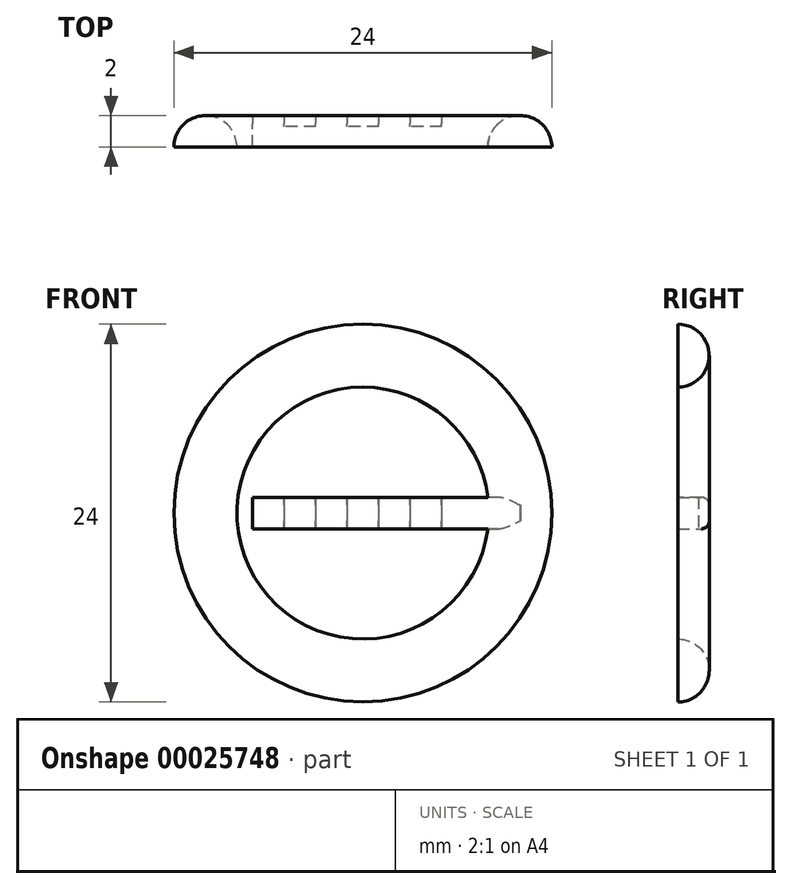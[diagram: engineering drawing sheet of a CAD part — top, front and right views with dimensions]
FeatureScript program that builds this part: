
annotation { "Feature Type Name" : "Feature", "Feature Type Description" : "" }
export const myFeature = defineFeature(function(context is Context, id is Id, definition is map)
    precondition{}
    {
        {
            var Q0;
            Q0=qCreatedBy(makeId("Top.planeOp"),FACE);
            var sketch = newSketch(context, id + "F0", { "sketchPlane" : qUnion([Q0])});
            skLineSegment(sketch, "E0", {"start": v(-2, 0) * mm, "end": v(2, 0) * mm});
            skArc(sketch, "E1", {"start": v(2, 0) * mm, "mid": v(0, 2) * mm, "end": v(-2, 0) * mm});
            skLineSegment(sketch, "E2", {"start": v(0, 0) * mm, "end": v(-17, 0) * mm});
            skSolve(sketch);
        }
        {
            var Q0;
            Q0=qCreatedBy(makeId("Front.planeOp"),FACE);
            var sketch = newSketch(context, id + "F1", { "sketchPlane" : qUnion([Q0])});
            skLineSegment(sketch, "E3", {"start": v(0, 0) * mm, "end": v(-20, 0) * mm, "construction": true});
            skCircle(sketch, "E4", {"center": v(-10, 0) * mm, "radius": 10 * mm, "construction": true});
            skSolve(sketch);
        }
        {
            var Q0;
            Q0=qCreatedBy(makeId("Right.planeOp"),FACE);
            var sketch = newSketch(context, id + "F2", { "sketchPlane" : qUnion([Q0])});
            skLineSegment(sketch, "E5.bottom", {"start": v(0, 1) * mm, "end": v(1.5, 1) * mm});
            skLineSegment(sketch, "E5.top", {"start": v(0, -1) * mm, "end": v(1.5, -1) * mm});
            skLineSegment(sketch, "E5.left", {"start": v(0, 1) * mm, "end": v(0, -1) * mm});
            skLineSegment(sketch, "E5.right", {"start": v(2, 0.5) * mm, "end": v(2, -0.5) * mm});
            skPoint(sketch, "E6.visualSharp", {"position": v(2, -1) * mm});
            skArc(sketch, "E6.filletArc", {"start": v(1.5, -1) * mm, "mid": v(1.85, -0.85) * mm, "end": v(2, -0.5) * mm});
            skPoint(sketch, "E7.visualSharp", {"position": v(2, 1) * mm});
            skArc(sketch, "E7.filletArc", {"start": v(2, 0.5) * mm, "mid": v(1.85, 0.85) * mm, "end": v(1.5, 1) * mm});
            skSolve(sketch);
        }
        {
            var Q0;
            {var subQ2=sQuery(id+"F0.wireOp",EDGE,"E0");Q0=makeQuery(id+"F0.imprint","IMPRINT",FACE,{"disambiguationData":[TD([[makeQuery(id+"F0.imprint","IMPRINT",EDGE,{"derivedFrom":subQ2}),1.0]])]});}
            var Q1;
            Q1=sQuery(id+"F0.wireOp",EDGE,"E1");
            var Q2;
            Q2=sQuery(id+"F0.wireOp",EDGE,"E0");
            var Q3;
            Q3=sQuery(id+"F1.wireOp",EDGE,"E4");
            revolve(context, id + "F3", {"entities" : qUnion([Q0]), "surfaceEntities" : qUnion([Q1, Q2]), "axis" : qUnion([Q3]), "revolveType" : RevolveType.FULL});
        }
        {
            var Q0;
            Q0 = qSketchRegion(id + "F2", true);
            var Q1;
            Q1=sQuery(id+"F0.wireOp",EDGE,"E2");
            sweep(context, id + "F4", {"operationType" : NewBodyOperationType.ADD, "profiles" : qUnion([Q0]), "path" : qUnion([Q1])});
        }
        {
            var Q0;
            Q0=makeQuery(id+"F4.opSweep","SWEPT_FACE",FACE,{"disambiguationData":[OSD([sQuery(id+"F0.wireOp",EDGE,"E2"),sQuery(id+"F2.wireOp",EDGE,"E5.right")])]});
            var sketch = newSketch(context, id + "F5", { "sketchPlane" : qUnion([Q0])});
            skLineSegment(sketch, "E8.rect.bottom", {"start": v(5, 1) * mm, "end": v(7, 1) * mm});
            skLineSegment(sketch, "E8.rect.top", {"start": v(5, -1) * mm, "end": v(7, -1) * mm});
            skLineSegment(sketch, "E8.rect.left", {"start": v(5, 1) * mm, "end": v(5, -1) * mm});
            skLineSegment(sketch, "E8.rect.right", {"start": v(7, 1) * mm, "end": v(7, -1) * mm});
            skPoint(sketch, "E8.rect.middle", {"position": v(6, 0) * mm});
            skLineSegment(sketch, "E9", {"start": v(0, 0) * mm, "end": v(6, 0) * mm, "construction": true});
            skLineSegment(sketch, "E10.1.0.0", {"start": v(9, 1) * mm, "end": v(9, -1) * mm});
            skLineSegment(sketch, "E10.1.0.1", {"start": v(9, 1) * mm, "end": v(11, 1) * mm});
            skPoint(sketch, "E10.1.0.2", {"position": v(10, 0) * mm});
            skLineSegment(sketch, "E10.1.0.3", {"start": v(11, 1) * mm, "end": v(11, -1) * mm});
            skLineSegment(sketch, "E10.1.0.4", {"start": v(9, -1) * mm, "end": v(11, -1) * mm});
            skLineSegment(sketch, "E10.2.0.0", {"start": v(13, 1) * mm, "end": v(13, -1) * mm});
            skLineSegment(sketch, "E10.2.0.1", {"start": v(13, 1) * mm, "end": v(15, 1) * mm});
            skPoint(sketch, "E10.2.0.2", {"position": v(14, 0) * mm});
            skLineSegment(sketch, "E10.2.0.3", {"start": v(15, 1) * mm, "end": v(15, -1) * mm});
            skLineSegment(sketch, "E10.2.0.4", {"start": v(13, -1) * mm, "end": v(15, -1) * mm});
            skLineSegment(sketch, "E10.direction1", {"start": v(5, -1) * mm, "end": v(9, -1) * mm, "construction": true});
            skSolve(sketch);
        }
        {
            var Q0;
            Q0 = qSketchRegion(id + "F5", true);
            extrude(context, id + "F6", {"entities" : qUnion([Q0]), "operationType" : NewBodyOperationType.REMOVE, "oppositeDirection" : true, "depth" : 0.7 * mm});
        }
    });
